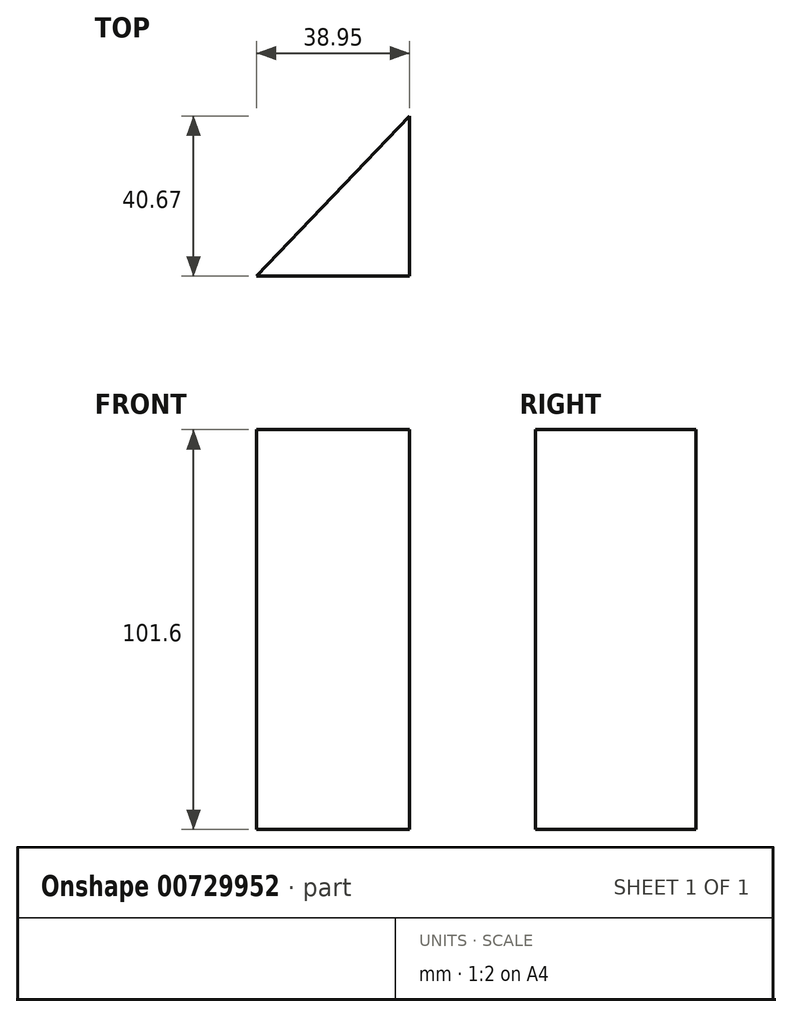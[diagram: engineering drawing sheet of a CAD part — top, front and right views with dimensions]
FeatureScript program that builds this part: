
annotation { "Feature Type Name" : "Feature", "Feature Type Description" : "" }
export const myFeature = defineFeature(function(context is Context, id is Id, definition is map)
    precondition{}
    {
        {
            var Q0;
            Q0=qCreatedBy(makeId("Top.planeOp"),FACE);
            var sketch = newSketch(context, id + "F0", { "sketchPlane" : qUnion([Q0])});
            skLineSegment(sketch, "E0", {"start": v(0, 0) * mm, "end": v(0, 40.67) * mm});
            skLineSegment(sketch, "E1", {"start": v(0, 40.67) * mm, "end": v(-38.95, 0) * mm});
            skLineSegment(sketch, "E2", {"start": v(-38.95, 0) * mm, "end": v(0, 0) * mm});
            skSolve(sketch);
        }
        {
            var Q0;
            Q0=makeQuery(id+"F0.imprint","IMPRINT",FACE,{"disambiguationData":[TD([[makeQuery(id+"F0.imprint","IMPRINT",EDGE,{"derivedFrom":sQuery(id+"F0.wireOp",EDGE,"E0")}),1.0]])]});
            extrude(context, id + "F1", {"entities" : qUnion([Q0]), "depth" : 101.6 * mm, "offsetDistance" : 25.4 * mm});
        }
    });
